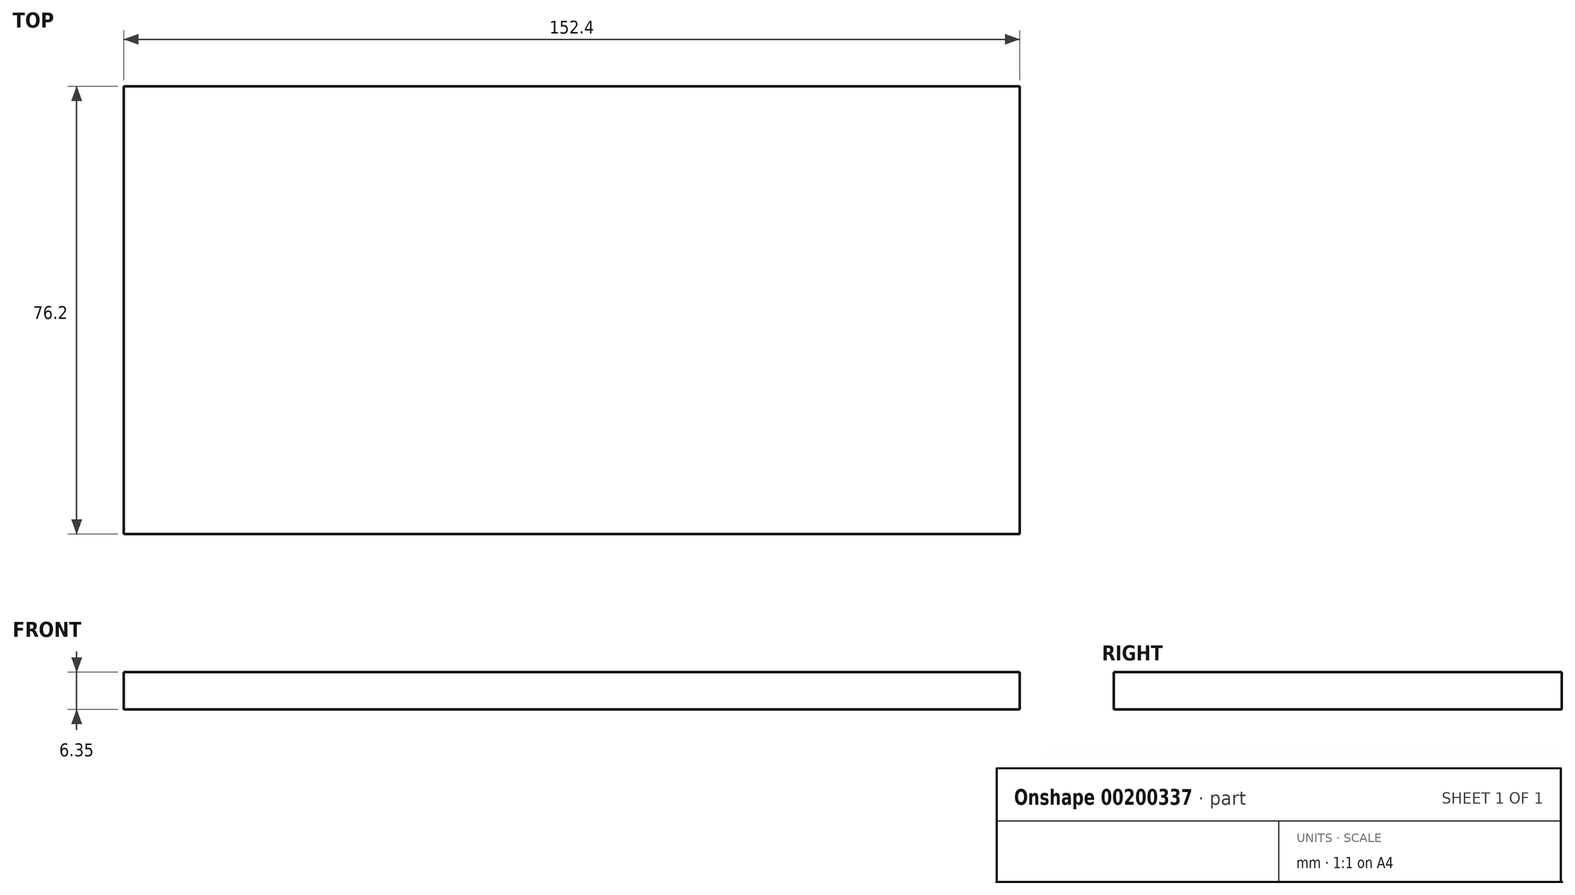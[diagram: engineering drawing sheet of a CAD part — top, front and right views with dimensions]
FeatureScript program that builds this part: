
annotation { "Feature Type Name" : "Feature", "Feature Type Description" : "" }
export const myFeature = defineFeature(function(context is Context, id is Id, definition is map)
    precondition{}
    {
        {
            var Q0;
            Q0=qCreatedBy(makeId("Top.planeOp"),FACE);
            var sketch = newSketch(context, id + "F0", { "sketchPlane" : qUnion([Q0])});
            skLineSegment(sketch, "E0.bottom", {"start": v(76.2, -38.1) * mm, "end": v(-76.2, -38.1) * mm});
            skLineSegment(sketch, "E0.top", {"start": v(76.2, 38.1) * mm, "end": v(-76.2, 38.1) * mm});
            skLineSegment(sketch, "E0.left", {"start": v(76.2, -38.1) * mm, "end": v(76.2, 38.1) * mm});
            skLineSegment(sketch, "E0.right", {"start": v(-76.2, -38.1) * mm, "end": v(-76.2, 38.1) * mm});
            skPoint(sketch, "E0.middle", {"position": v(0, 0) * mm});
            skSolve(sketch);
        }
        {
            var Q0;
            Q0=makeQuery(id+"F0.imprint","IMPRINT",FACE,{"disambiguationData":[TD([[makeQuery(id+"F0.imprint","IMPRINT",EDGE,{"derivedFrom":sQuery(id+"F0.wireOp",EDGE,"E0.bottom")}),-1.0]])]});
            extrude(context, id + "F1", {"entities" : qUnion([Q0]), "depth" : 6.35 * mm});
        }
    });
